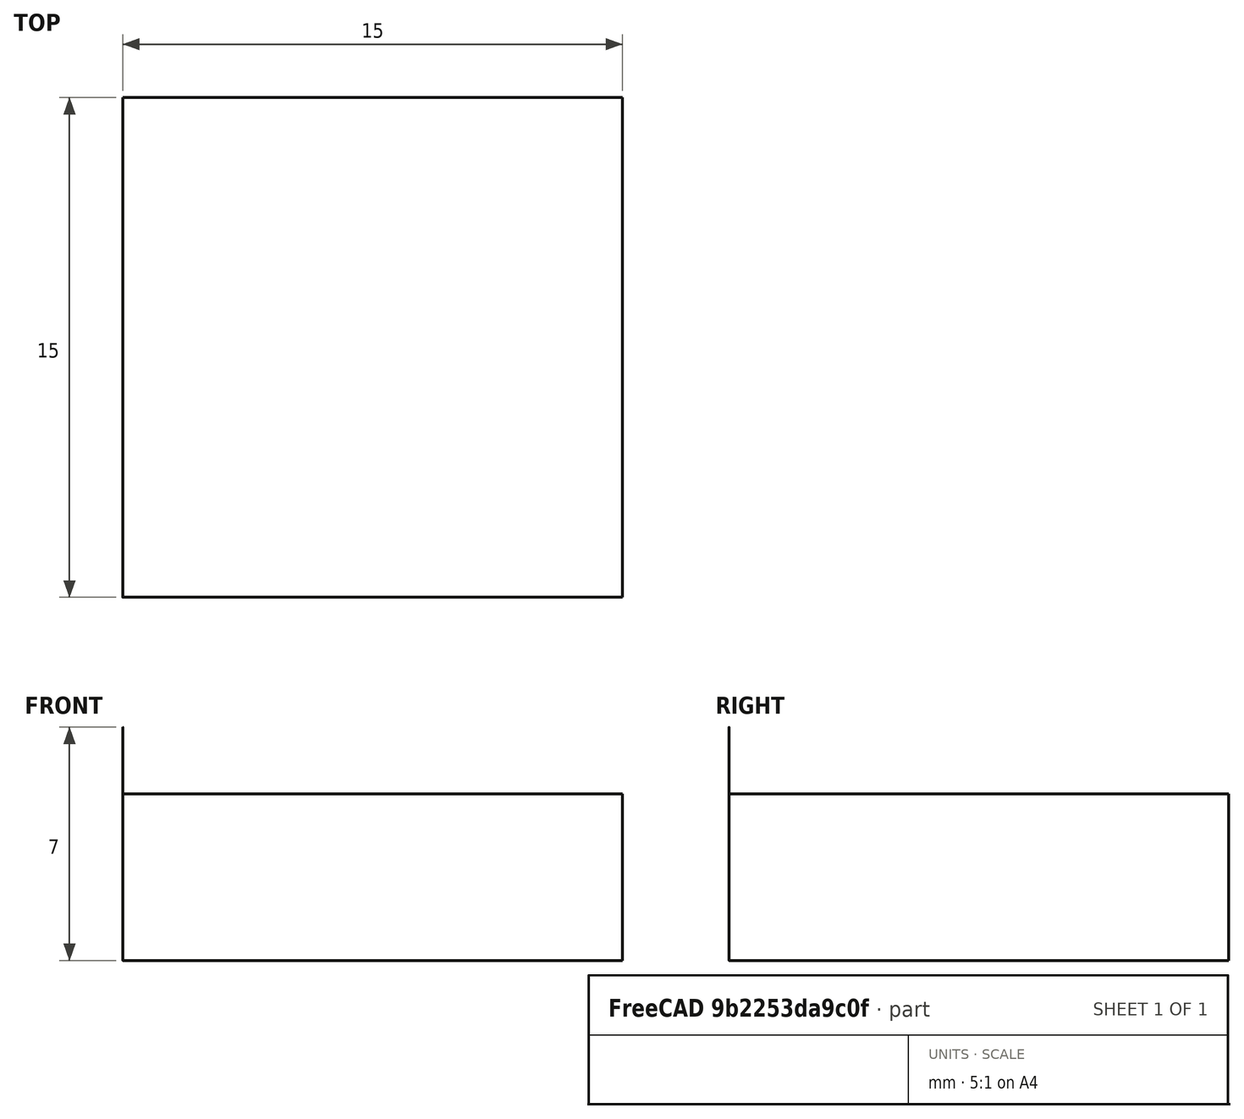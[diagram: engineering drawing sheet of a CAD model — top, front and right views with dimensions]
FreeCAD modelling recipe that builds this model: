
FCSTD DOCUMENT  (FreeCAD 1.0R39109 (Git))
Label: BoxWith9GridPockets
License: All rights reserved
LicenseURL: https://en.wikipedia.org/wiki/All_rights_reserved
objects: Part::Box×10, Part::Cut×9, Part::FeaturePython×3, App::DocumentObjectGroup×3, Path::FeaturePython×3, App::FeaturePython×1
note: 23 computed .brp shape members not serialized (recipe doc carries the construction recipe); baked Part::Feature solids carry a one-line shape summary decoded from their .brp

FEATURE [Part::Box] Box
  AttacherType = Attacher::AttachEngine3D
  Height = 5
  Length = 15
  Width = 15
FEATURE [Part::Box] Pocket_0_0
  AttacherType = Attacher::AttachEngine3D
  Height = 0.05
  Length = 0.2
  Placement = pos=(3.6,3.6,4.95) rot=(0,0,1;0rad)
  Width = 0.2
FEATURE [Part::Box] Pocket_0_1
  AttacherType = Attacher::AttachEngine3D
  Height = 0.05
  Length = 0.2
  Placement = pos=(7.4,3.6,4.95) rot=(0,0,1;0rad)
  Width = 0.2
FEATURE [Part::Box] Pocket_0_2
  AttacherType = Attacher::AttachEngine3D
  Height = 0.05
  Length = 0.2
  Placement = pos=(11.2,3.6,4.95) rot=(0,0,1;0rad)
  Width = 0.2
FEATURE [Part::Box] Pocket_1_0
  AttacherType = Attacher::AttachEngine3D
  Height = 0.05
  Length = 0.2
  Placement = pos=(3.6,7.4,4.95) rot=(0,0,1;0rad)
  Width = 0.2
FEATURE [Part::Box] Pocket_1_1
  AttacherType = Attacher::AttachEngine3D
  Height = 0.05
  Length = 0.2
  Placement = pos=(7.4,7.4,4.95) rot=(0,0,1;0rad)
  Width = 0.2
FEATURE [Part::Box] Pocket_1_2
  AttacherType = Attacher::AttachEngine3D
  Height = 0.05
  Length = 0.2
  Placement = pos=(11.2,7.4,4.95) rot=(0,0,1;0rad)
  Width = 0.2
FEATURE [Part::Box] Pocket_2_0
  AttacherType = Attacher::AttachEngine3D
  Height = 0.05
  Length = 0.2
  Placement = pos=(3.6,11.2,4.95) rot=(0,0,1;0rad)
  Width = 0.2
FEATURE [Part::Box] Pocket_2_1
  AttacherType = Attacher::AttachEngine3D
  Height = 0.05
  Length = 0.2
  Placement = pos=(7.4,11.2,4.95) rot=(0,0,1;0rad)
  Width = 0.2
FEATURE [Part::Box] Pocket_2_2
  AttacherType = Attacher::AttachEngine3D
  Height = 0.05
  Length = 0.2
  Placement = pos=(11.2,11.2,4.95) rot=(0,0,1;0rad)
  Width = 0.2
FEATURE [Part::Cut] Cut  label="Cut_0"
  Base = -> Box
  Refine = true
  Tool = -> Pocket_0_0
FEATURE [Part::Cut] Cut001  label="Cut_1"
  Base = -> Cut
  Refine = true
  Tool = -> Pocket_0_1
FEATURE [Part::Cut] Cut002  label="Cut_2"
  Base = -> Cut001
  Refine = true
  Tool = -> Pocket_0_2
FEATURE [Part::Cut] Cut003  label="Cut_3"
  Base = -> Cut002
  Refine = true
  Tool = -> Pocket_1_0
FEATURE [Part::Cut] Cut004  label="Cut_4"
  Base = -> Cut003
  Refine = true
  Tool = -> Pocket_1_1
FEATURE [Part::Cut] Cut005  label="Cut_5"
  Base = -> Cut004
  Refine = true
  Tool = -> Pocket_1_2
FEATURE [Part::Cut] Cut006  label="Cut_6"
  Base = -> Cut005
  Refine = true
  Tool = -> Pocket_2_0
FEATURE [Part::Cut] Cut007  label="Cut_7"
  Base = -> Cut006
  Refine = true
  Tool = -> Pocket_2_1
FEATURE [Part::Cut] Cut008  label="Cut_8"
  Base = -> Cut007
  Refine = true
  Tool = -> Pocket_2_2
FEATURE [App::FeaturePython] SetupSheet  # Path/CAM operation (typed FeaturePython)
  ClearanceHeightExpression = OpStockZMax+SetupSheet.ClearanceHeightOffset
  ClearanceHeightOffset = 5
  CoolantMode = 0
  CoolantModes = None | Flood | Mist
  FinalDepthExpression = OpFinalDepth
  HorizRapid = 333.333
  SafeHeightExpression = OpStockZMax+SetupSheet.SafeHeightOffset
  SafeHeightOffset = 3
  StartDepthExpression = OpStartDepth
  StepDownExpression = OpToolDiameter
  VertRapid = 0
FEATURE [Part::FeaturePython] Clone  label="Model-Cut_8"  # Draft clone (typed FeaturePython)
  AttacherType = Attacher::AttachEngine3D
  Fuse = false
  Objects = -> [Cut008]
  PathResource = Model
  Scale = (1,1,1)
FEATURE [App::DocumentObjectGroup] Model
  Group = -> [Clone]
FEATURE [Part::FeaturePython] ToolBit  label="Drill"  # Path/CAM toolbit (typed FeaturePython)
  BitPropertyNames = Chipload | Diameter | Flutes | Length | Material | TipAngle
  BitShape = <path>
  Chipload = 0
  Diameter = 0.005
  Flutes = 0
  Length = 7
  Material = 0
  ShapeName = drill
  TipAngle = 119
FEATURE [Path::FeaturePython] TC__Default_Tool  label="TC: Default Tool"  # Path/CAM operation (typed FeaturePython)
  HorizFeed = 0
  HorizRapid = 333.333
  SpindleDir = 0
  SpindleSpeed = 0
  Tool = -> ToolBit
  ToolNumber = 1
  VertFeed = 0
  VertRapid = 0
  expr: HorizRapid = SetupSheet.HorizRapid
  expr: VertRapid = SetupSheet.VertRapid
FEATURE [App::DocumentObjectGroup] Tools
  Group = -> [TC__Default_Tool]
FEATURE [Part::FeaturePython] Stock  # WARN: FeaturePython — macro-defined, semantics opaque (R4)
  Base = -> Model
  ExtXneg = 0.001
  ExtXpos = 0.001
  ExtYneg = 0.001
  ExtYpos = 0.001
  ExtZneg = 0.001
  ExtZpos = 0.001
  StockType = FromBase
FEATURE [Path::FeaturePython] Pocket_Shape  # Path/CAM operation (typed FeaturePython)
  Active = true
  AreaParams:
    Tolerance = 1e-07
    FitArcs = True
    Simplify = False
    CleanDistance = 0.0
    Accuracy = 0.01
    Unit = 1.0
    MinArcPoints = 4
    MaxArcPoints = 100
    ClipperScale = 10000000.0
    Fill = 0
    Coplanar = 0
    Reorient = True
    Outline = False
    Explode = False
    OpenMode = 0
    Deflection = 0.01
    SubjectFill = 0
    ClipFill = 0
    Offset = 0.0
    ExtraPass = 0
    Stepover = 0.0
    LastStepover = 0.0
    JoinType = 0
    EndType = 0
    MiterLimit = 2.0
    RoundPrecision = 0.0
    PocketMode = 1
    ToolRadius = 0.0025
    PocketExtraOffset = 0.0
    PocketStepover = 0.0025
    PocketLastStepover = 0.0
    FromCenter = True
    Angle = 0.0
    AngleShift = 0.0
    Shift = 0.0
    Thicken = False
    SectionCount = -1
    Stepdown = 1.0
    SectionOffset = 0.0
    SectionTolerance = 1e-06
    SectionMode = 2
    Project = False
  Base = -> [Clone]
  ClearanceHeight = 10.001
  CoolantMode = 0
  CutMode = 0
  CycleTime = Cycletime Error
  ExtensionCorners = true
  ExtensionLengthDefault = 0.0025
  ExtraOffset = 0
  FinalDepth = 4.95
  FinishDepth = 0
  KeepToolDown = false
  MinTravel = false
  OffsetPattern = 0
  OpFinalDepth = 4.95
  OpStartDepth = 5.001
  OpStockZMax = 5.001
  OpStockZMin = -0.001
  OpToolDiameter = 0.005
  PathParams = {'orientation': 1, 'feedrate': 0.0, 'feedrate_v': 0.0, 'verbose': True, 'resume_height': 8.001000000000001, 'retraction': 10.001000000000001, 'return_end': True, 'preamble': False, 'start': Vector (11.397499900000001, 7.597499900000001, 10.001000000000001)}
  PocketLastStepOver = 0
  SafeHeight = 8.001
  SplitArcs = false
  StartAt = 0
  StartDepth = 5.001
  StartPoint = (0,0,0)
  StepDown = 0.005
  StepOver = 50
  ToolController = -> TC__Default_Tool
  UseOutline = false
  UseRestMachining = false
  UseStartPoint = false
  ZigZagAngle = 0
  expr: ClearanceHeight = OpStockZMax + SetupSheet.ClearanceHeightOffset
  expr: ExtensionLengthDefault = OpToolDiameter / 2
  expr: FinalDepth = OpFinalDepth
  expr: SafeHeight = OpStockZMax + SetupSheet.SafeHeightOffset
  expr: StartDepth = OpStartDepth
  expr: StepDown = OpToolDiameter
FEATURE [App::DocumentObjectGroup] Operations
  Group = -> [Pocket_Shape]
FEATURE [Path::FeaturePython] Job  # Path/CAM operation (typed FeaturePython)
  CycleTime = 00:00:00
  Fixtures = G54
  GeometryTolerance = 0.01
  JobType = 0
  Model = -> Model
  Operations = -> Operations
  OrderOutputBy = 0
  PostProcessor = 14
  PostProcessorOutputFile = <userpath>/Desktop/freecad/laser.gcode
  SetupSheet = -> SetupSheet
  SplitOutput = false
  Stock = -> Stock
  Tools = -> Tools
note: 1 file-system path scrubbed to <path> (originals preserved in the JSON sidecar)
